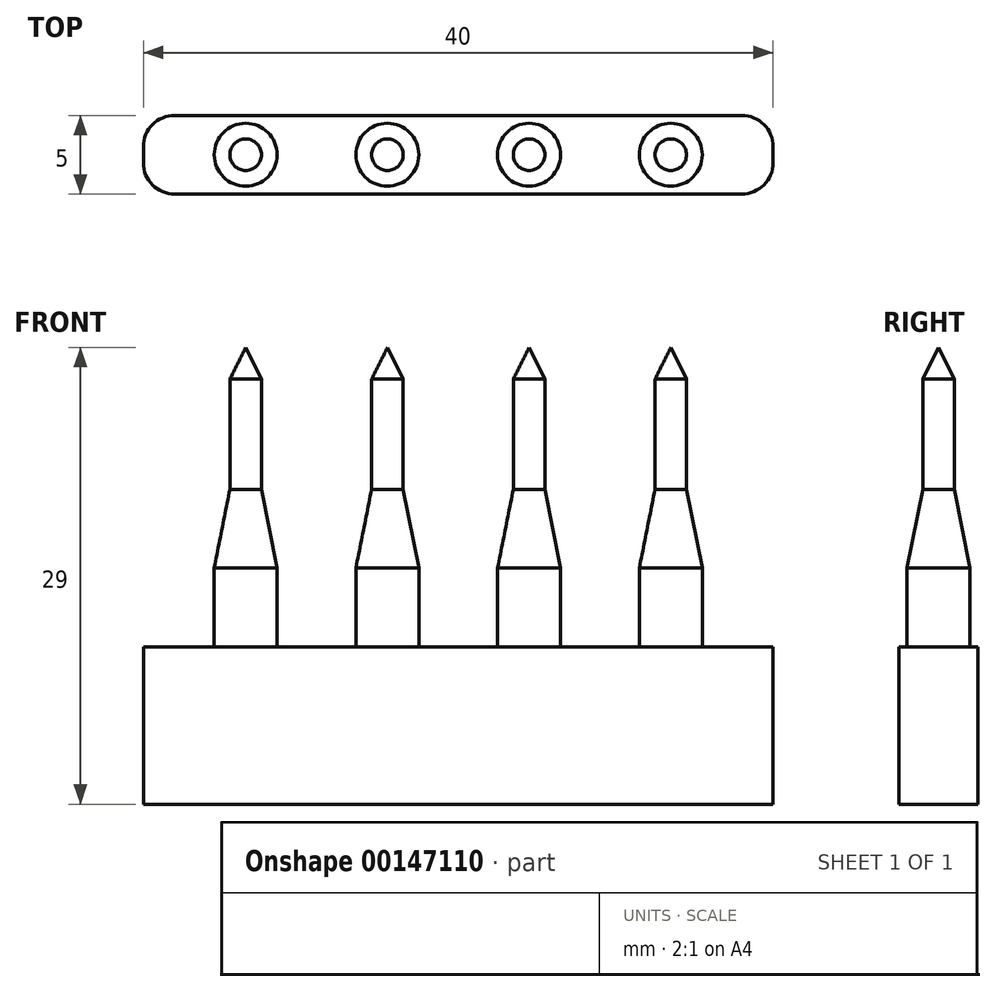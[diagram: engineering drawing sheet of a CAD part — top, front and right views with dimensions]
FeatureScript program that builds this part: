
annotation { "Feature Type Name" : "Feature", "Feature Type Description" : "" }
export const myFeature = defineFeature(function(context is Context, id is Id, definition is map)
    precondition{}
    {
        {
            var Q0;
            Q0=qCreatedBy(makeId("Top.planeOp"),FACE);
            var sketch = newSketch(context, id + "F0", { "sketchPlane" : qUnion([Q0])});
            skLineSegment(sketch, "E0", {"start": v(0, 0) * mm, "end": v(4.5, 0) * mm});
            skLineSegment(sketch, "E1", {"start": v(4.5, 0) * mm, "end": v(13.5, 0) * mm});
            skLineSegment(sketch, "E2", {"start": v(0, 0) * mm, "end": v(-4.5, 0) * mm});
            skLineSegment(sketch, "E3", {"start": v(-4.5, 0) * mm, "end": v(-13.5, 0) * mm});
            skCircle(sketch, "E4", {"center": v(-13.5, 0) * mm, "radius": 1 * mm});
            skCircle(sketch, "E5", {"center": v(-4.5, 0) * mm, "radius": 1 * mm});
            skCircle(sketch, "E6", {"center": v(4.5, 0) * mm, "radius": 1 * mm});
            skCircle(sketch, "E7", {"center": v(13.5, 0) * mm, "radius": 1 * mm});
            skLineSegment(sketch, "E8.bottom", {"start": v(20, 2.5) * mm, "end": v(-20, 2.5) * mm});
            skLineSegment(sketch, "E8.top", {"start": v(20, -2.5) * mm, "end": v(-20, -2.5) * mm});
            skLineSegment(sketch, "E8.left", {"start": v(20, 2.5) * mm, "end": v(20, -2.5) * mm});
            skLineSegment(sketch, "E8.right", {"start": v(-20, 2.5) * mm, "end": v(-20, -2.5) * mm});
            skPoint(sketch, "E8.middle", {"position": v(0, 0) * mm});
            skCircle(sketch, "E9", {"center": v(-13.5, 0) * mm, "radius": 2 * mm});
            skCircle(sketch, "E10", {"center": v(-4.5, 0) * mm, "radius": 2 * mm});
            skCircle(sketch, "E11", {"center": v(4.5, 0) * mm, "radius": 2 * mm});
            skCircle(sketch, "E12", {"center": v(13.5, 0) * mm, "radius": 2 * mm});
            skSolve(sketch);
        }
        {
            var Q0;
            {var subQ0=sQuery(id+"F0.wireOp",EDGE,"E8.left");Q0=makeQuery(id+"F0.imprint","IMPRINT",FACE,{"disambiguationData":[TD([[makeQuery(id+"F0.imprint","IMPRINT",EDGE,{"derivedFrom":subQ0}),-1.0]])]});}
            var Q1;
            {var subQ0=sQuery(id+"F0.wireOp",EDGE,"E8.right");Q1=makeQuery(id+"F0.imprint","IMPRINT",FACE,{"disambiguationData":[TD([[makeQuery(id+"F0.imprint","IMPRINT",EDGE,{"derivedFrom":subQ0}),1.0]])]});}
            var Q2;
            {var subQ3=sQuery(id+"F0.wireOp",EDGE,"E2");var subQ5=sQuery(id+"F0.wireOp",EDGE,"E0");var subQ6=makeQuery(id+"F0.imprint","INTERSECT",VERTEX,{"derivedFrom":[subQ5,subQ3]});Q2=makeQuery(id+"F0.imprint","IMPRINT",FACE,{"disambiguationData":[TD([[makeQuery(id+"F0.imprint","IMPRINT",EDGE,{"disambiguationData":[TD([[subQ6,-1.0]])],"derivedFrom":subQ5}),1.0]])]});}
            var Q3;
            {var subQ3=sQuery(id+"F0.wireOp",EDGE,"E2");var subQ7=sQuery(id+"F0.wireOp",EDGE,"E0");var subQ8=makeQuery(id+"F0.imprint","INTERSECT",VERTEX,{"derivedFrom":[subQ7,subQ3]});Q3=makeQuery(id+"F0.imprint","IMPRINT",FACE,{"disambiguationData":[TD([[makeQuery(id+"F0.imprint","IMPRINT",EDGE,{"disambiguationData":[TD([[subQ8,-1.0]])],"derivedFrom":subQ7}),-1.0]])]});}
            var Q4;
            {var subQ0=sQuery(id+"F0.wireOp",EDGE,"U3uNiEoL-ytFB-zz6d-zu6e-E4LWmO1OLc1b");var subQ1=sQuery(id+"F0.wireOp",EDGE,"E1");var subQ2=makeQuery(id+"F0.imprint","INTERSECT",VERTEX,{"derivedFrom":[subQ1,subQ0]});Q4=makeQuery(id+"F0.imprint","IMPRINT",FACE,{"disambiguationData":[TD([[makeQuery(id+"F0.imprint","IMPRINT",EDGE,{"disambiguationData":[TD([[subQ2,1.0]])],"derivedFrom":subQ1}),1.0]])]});}
            var Q5;
            {var subQ0=sQuery(id+"F0.wireOp",EDGE,"U3uNiEoL-ytFB-zz6d-zu6e-E4LWmO1OLc1b");var subQ1=sQuery(id+"F0.wireOp",EDGE,"E1");var subQ2=makeQuery(id+"F0.imprint","INTERSECT",VERTEX,{"derivedFrom":[subQ1,subQ0]});Q5=makeQuery(id+"F0.imprint","IMPRINT",FACE,{"disambiguationData":[TD([[makeQuery(id+"F0.imprint","IMPRINT",EDGE,{"disambiguationData":[TD([[subQ2,1.0]])],"derivedFrom":subQ1}),-1.0]])]});}
            var Q6;
            {var subQ0=sQuery(id+"F0.wireOp",EDGE,"ClDRhj1H-6xjR-YOIk-xAHQ-ztIX2t5JyYzg");var subQ1=sQuery(id+"F0.wireOp",EDGE,"E3");var subQ2=makeQuery(id+"F0.imprint","INTERSECT",VERTEX,{"derivedFrom":[subQ1,subQ0]});Q6=makeQuery(id+"F0.imprint","IMPRINT",FACE,{"disambiguationData":[TD([[makeQuery(id+"F0.imprint","IMPRINT",EDGE,{"disambiguationData":[TD([[subQ2,1.0]])],"derivedFrom":subQ1}),-1.0]])]});}
            var Q7;
            {var subQ0=sQuery(id+"F0.wireOp",EDGE,"ClDRhj1H-6xjR-YOIk-xAHQ-ztIX2t5JyYzg");var subQ1=sQuery(id+"F0.wireOp",EDGE,"E3");var subQ2=makeQuery(id+"F0.imprint","INTERSECT",VERTEX,{"derivedFrom":[subQ1,subQ0]});Q7=makeQuery(id+"F0.imprint","IMPRINT",FACE,{"disambiguationData":[TD([[makeQuery(id+"F0.imprint","IMPRINT",EDGE,{"disambiguationData":[TD([[subQ2,1.0]])],"derivedFrom":subQ1}),1.0]])]});}
            var Q8;
            Q8=makeQuery(id+"F0.imprint","IMPRINT",FACE,{"disambiguationData":[TD([[makeQuery(id+"F0.imprint","IMPRINT",EDGE,{"derivedFrom":sQuery(id+"F0.wireOp",EDGE,"E7")}),-1.0]])]});
            var Q9;
            {var subQ0=sQuery(id+"F0.wireOp",EDGE,"8HZm2u9n-6hcU-8h6m-0SvE-3ht0zT66AFrF");var subQ2=sQuery(id+"F0.wireOp",EDGE,"E0");var subQ3=makeQuery(id+"F0.imprint","INTERSECT",VERTEX,{"derivedFrom":[subQ2,subQ0]});Q9=makeQuery(id+"F0.imprint","IMPRINT",FACE,{"disambiguationData":[TD([[makeQuery(id+"F0.imprint","IMPRINT",EDGE,{"disambiguationData":[TD([[subQ3,-1.0]])],"derivedFrom":subQ2}),-1.0]])]});}
            var Q10;
            {var subQ1=sQuery(id+"F0.wireOp",EDGE,"E2");var subQ5=sQuery(id+"F0.wireOp",EDGE,"egIFAelI-ejJv-sLzS-e5zb-D6Cz2TTPKjOq");var subQ7=makeQuery(id+"F0.imprint","INTERSECT",VERTEX,{"derivedFrom":[subQ1,subQ5]});Q10=makeQuery(id+"F0.imprint","IMPRINT",FACE,{"disambiguationData":[TD([[makeQuery(id+"F0.imprint","IMPRINT",EDGE,{"disambiguationData":[TD([[subQ7,-1.0]])],"derivedFrom":subQ1}),1.0]])]});}
            var Q11;
            Q11=makeQuery(id+"F0.imprint","IMPRINT",FACE,{"disambiguationData":[TD([[makeQuery(id+"F0.imprint","IMPRINT",EDGE,{"derivedFrom":sQuery(id+"F0.wireOp",EDGE,"E4")}),-1.0]])]});
            var Q12;
            {var subQ0=sQuery(id+"F0.wireOp",EDGE,"egIFAelI-ejJv-sLzS-e5zb-D6Cz2TTPKjOq");var subQ2=sQuery(id+"F0.wireOp",EDGE,"E2");var subQ3=makeQuery(id+"F0.imprint","INTERSECT",VERTEX,{"derivedFrom":[subQ2,subQ0]});Q12=makeQuery(id+"F0.imprint","IMPRINT",FACE,{"disambiguationData":[TD([[makeQuery(id+"F0.imprint","IMPRINT",EDGE,{"disambiguationData":[TD([[subQ3,-1.0]])],"derivedFrom":subQ2}),-1.0]])]});}
            var Q13;
            {var subQ0=sQuery(id+"F0.wireOp",EDGE,"8HZm2u9n-6hcU-8h6m-0SvE-3ht0zT66AFrF");var subQ5=sQuery(id+"F0.wireOp",EDGE,"E0");var subQ8=makeQuery(id+"F0.imprint","INTERSECT",VERTEX,{"derivedFrom":[subQ5,subQ0]});Q13=makeQuery(id+"F0.imprint","IMPRINT",FACE,{"disambiguationData":[TD([[makeQuery(id+"F0.imprint","IMPRINT",EDGE,{"disambiguationData":[TD([[subQ8,-1.0]])],"derivedFrom":subQ5}),1.0]])]});}
            var Q14;
            Q14=makeQuery(id+"F0.imprint","IMPRINT",FACE,{"disambiguationData":[TD([[makeQuery(id+"F0.imprint","IMPRINT",EDGE,{"derivedFrom":sQuery(id+"F0.wireOp",EDGE,"E7")}),1.0]])]});
            var Q15;
            {var subQ0=sQuery(id+"F0.wireOp",EDGE,"E1");var subQ1=sQuery(id+"F0.wireOp",EDGE,"E0");var subQ2=makeQuery(id+"F0.imprint","INTERSECT",VERTEX,{"derivedFrom":[subQ1,subQ0]});Q15=makeQuery(id+"F0.imprint","IMPRINT",FACE,{"disambiguationData":[TD([[makeQuery(id+"F0.imprint","IMPRINT",EDGE,{"disambiguationData":[TD([[subQ2,1.0]])],"derivedFrom":subQ1}),-1.0]])]});}
            var Q16;
            {var subQ0=sQuery(id+"F0.wireOp",EDGE,"E3");var subQ1=sQuery(id+"F0.wireOp",EDGE,"E2");var subQ2=makeQuery(id+"F0.imprint","INTERSECT",VERTEX,{"derivedFrom":[subQ1,subQ0]});Q16=makeQuery(id+"F0.imprint","IMPRINT",FACE,{"disambiguationData":[TD([[makeQuery(id+"F0.imprint","IMPRINT",EDGE,{"disambiguationData":[TD([[subQ2,1.0]])],"derivedFrom":subQ1}),1.0]])]});}
            var Q17;
            Q17=makeQuery(id+"F0.imprint","IMPRINT",FACE,{"disambiguationData":[TD([[makeQuery(id+"F0.imprint","IMPRINT",EDGE,{"derivedFrom":sQuery(id+"F0.wireOp",EDGE,"E4")}),1.0]])]});
            var Q18;
            {var subQ0=sQuery(id+"F0.wireOp",EDGE,"E3");var subQ1=sQuery(id+"F0.wireOp",EDGE,"E2");var subQ2=makeQuery(id+"F0.imprint","INTERSECT",VERTEX,{"derivedFrom":[subQ1,subQ0]});Q18=makeQuery(id+"F0.imprint","IMPRINT",FACE,{"disambiguationData":[TD([[makeQuery(id+"F0.imprint","IMPRINT",EDGE,{"disambiguationData":[TD([[subQ2,1.0]])],"derivedFrom":subQ1}),-1.0]])]});}
            var Q19;
            {var subQ0=sQuery(id+"F0.wireOp",EDGE,"E1");var subQ1=sQuery(id+"F0.wireOp",EDGE,"E0");var subQ2=makeQuery(id+"F0.imprint","INTERSECT",VERTEX,{"derivedFrom":[subQ1,subQ0]});Q19=makeQuery(id+"F0.imprint","IMPRINT",FACE,{"disambiguationData":[TD([[makeQuery(id+"F0.imprint","IMPRINT",EDGE,{"disambiguationData":[TD([[subQ2,1.0]])],"derivedFrom":subQ1}),1.0]])]});}
            var Q20;
            {var subQ0=sQuery(id+"F0.wireOp",EDGE,"E10");var subQ1=sQuery(id+"F0.wireOp",EDGE,"E2");var subQ2=makeQuery(id+"F0.imprint","INTERSECT",VERTEX,{"derivedFrom":[subQ1,subQ0]});Q20=makeQuery(id+"F0.imprint","IMPRINT",FACE,{"disambiguationData":[TD([[makeQuery(id+"F0.imprint","IMPRINT",EDGE,{"disambiguationData":[TD([[subQ2,-1.0]])],"derivedFrom":subQ1}),1.0]])]});}
            var Q21;
            {var subQ0=sQuery(id+"F0.wireOp",EDGE,"E11");var subQ1=sQuery(id+"F0.wireOp",EDGE,"E0");var subQ2=makeQuery(id+"F0.imprint","INTERSECT",VERTEX,{"derivedFrom":[subQ1,subQ0]});Q21=makeQuery(id+"F0.imprint","IMPRINT",FACE,{"disambiguationData":[TD([[makeQuery(id+"F0.imprint","IMPRINT",EDGE,{"disambiguationData":[TD([[subQ2,-1.0]])],"derivedFrom":subQ1}),-1.0]])]});}
            var Q22;
            {var subQ0=sQuery(id+"F0.wireOp",EDGE,"E11");var subQ1=sQuery(id+"F0.wireOp",EDGE,"E0");var subQ2=makeQuery(id+"F0.imprint","INTERSECT",VERTEX,{"derivedFrom":[subQ1,subQ0]});Q22=makeQuery(id+"F0.imprint","IMPRINT",FACE,{"disambiguationData":[TD([[makeQuery(id+"F0.imprint","IMPRINT",EDGE,{"disambiguationData":[TD([[subQ2,-1.0]])],"derivedFrom":subQ1}),1.0]])]});}
            var Q23;
            {var subQ0=sQuery(id+"F0.wireOp",EDGE,"E10");var subQ1=sQuery(id+"F0.wireOp",EDGE,"E2");var subQ2=makeQuery(id+"F0.imprint","INTERSECT",VERTEX,{"derivedFrom":[subQ1,subQ0]});Q23=makeQuery(id+"F0.imprint","IMPRINT",FACE,{"disambiguationData":[TD([[makeQuery(id+"F0.imprint","IMPRINT",EDGE,{"disambiguationData":[TD([[subQ2,-1.0]])],"derivedFrom":subQ1}),-1.0]])]});}
            extrude(context, id + "F1", {"entities" : qUnion([Q0, Q1, Q2, Q3, Q4, Q5, Q6, Q7, Q8, Q9, Q10, Q11, Q12, Q13, Q14, Q15, Q16, Q17, Q18, Q19, Q20, Q21, Q22, Q23]), "oppositeDirection" : true, "depth" : 10 * mm, "offsetDistance" : 25 * mm});
        }
        {
            var Q0;
            Q0=qCreatedBy(makeId("Front.planeOp"),FACE);
            var sketch = newSketch(context, id + "F2", { "sketchPlane" : qUnion([Q0])});
            skLineSegment(sketch, "E13", {"start": v(0, 0) * mm, "end": v(4.5, 0) * mm});
            skLineSegment(sketch, "E14", {"start": v(4.5, 0) * mm, "end": v(13.5, 0) * mm});
            skLineSegment(sketch, "E15", {"start": v(0, 0) * mm, "end": v(-4.5, 0) * mm});
            skLineSegment(sketch, "E16", {"start": v(-4.5, 0) * mm, "end": v(-13.5, 0) * mm});
            skLineSegment(sketch, "E17", {"start": v(-13.5, 0) * mm, "end": v(-13.5, 5) * mm});
            skLineSegment(sketch, "E18", {"start": v(-13.5, 5) * mm, "end": v(-11.5, 5) * mm});
            skLineSegment(sketch, "E19", {"start": v(-13.5, 5) * mm, "end": v(-13.5, 10) * mm});
            skLineSegment(sketch, "E20", {"start": v(-13.5, 10) * mm, "end": v(-12.5, 10) * mm});
            skLineSegment(sketch, "E21", {"start": v(-12.5, 10) * mm, "end": v(-11.5, 5) * mm});
            skLineSegment(sketch, "E22", {"start": v(-4.5, 0) * mm, "end": v(-4.5, 10) * mm});
            skLineSegment(sketch, "E23", {"start": v(-4.5, 10) * mm, "end": v(-3.5, 10) * mm});
            skLineSegment(sketch, "E24", {"start": v(-4.5, 0) * mm, "end": v(-4.5, 5) * mm});
            skLineSegment(sketch, "E25", {"start": v(-4.5, 5) * mm, "end": v(-2.5, 5) * mm});
            skLineSegment(sketch, "E26", {"start": v(-2.5, 5) * mm, "end": v(-3.5, 10) * mm});
            skLineSegment(sketch, "E27.MirrorCS", {"start": v(4.5, 5) * mm, "end": v(2.5, 5) * mm});
            skLineSegment(sketch, "E28.MirrorCS", {"start": v(2.5, 5) * mm, "end": v(3.5, 10) * mm});
            skLineSegment(sketch, "E29.MirrorCS", {"start": v(4.5, 10) * mm, "end": v(3.5, 10) * mm});
            skLineSegment(sketch, "E30", {"start": v(-12.5, 10) * mm, "end": v(-12.5, 17) * mm});
            skLineSegment(sketch, "E31", {"start": v(-13.5, 10) * mm, "end": v(-13.5, 19) * mm});
            skLineSegment(sketch, "E32", {"start": v(-13.5, 19) * mm, "end": v(-12.5, 17) * mm});
            skLineSegment(sketch, "E33", {"start": v(-4.5, 10) * mm, "end": v(-4.5, 19) * mm});
            skLineSegment(sketch, "E34", {"start": v(-3.5, 10) * mm, "end": v(-3.5, 17) * mm});
            skLineSegment(sketch, "E35", {"start": v(-3.5, 17) * mm, "end": v(-4.5, 19) * mm});
            skLineSegment(sketch, "E36.MirrorCS", {"start": v(3.5, 10) * mm, "end": v(3.5, 17) * mm});
            skLineSegment(sketch, "E37.MirrorCS", {"start": v(4.5, 10) * mm, "end": v(4.5, 19) * mm});
            skLineSegment(sketch, "E38.MirrorCS", {"start": v(3.5, 17) * mm, "end": v(4.5, 19) * mm});
            skLineSegment(sketch, "E39.MirrorCS", {"start": v(4.5, 0) * mm, "end": v(4.5, 10) * mm});
            skLineSegment(sketch, "E40.MirrorCS", {"start": v(13.5, 10) * mm, "end": v(13.5, 19) * mm});
            skLineSegment(sketch, "E41.MirrorCS", {"start": v(13.5, 19) * mm, "end": v(12.5, 17) * mm});
            skLineSegment(sketch, "E42.MirrorCS", {"start": v(12.5, 10) * mm, "end": v(12.5, 17) * mm});
            skLineSegment(sketch, "E43.MirrorCS", {"start": v(12.5, 10) * mm, "end": v(11.5, 5) * mm});
            skLineSegment(sketch, "E44.MirrorCS", {"start": v(13.5, 5) * mm, "end": v(13.5, 10) * mm});
            skLineSegment(sketch, "E45.MirrorCS", {"start": v(13.5, 5) * mm, "end": v(11.5, 5) * mm});
            skSolve(sketch);
        }
        {
            var Q0;
            Q0=makeQuery(id+"F0.imprint","IMPRINT",FACE,{"disambiguationData":[TD([[makeQuery(id+"F0.imprint","IMPRINT",EDGE,{"derivedFrom":sQuery(id+"F0.wireOp",EDGE,"E4")}),-1.0]])]});
            var Q1;
            {var subQ1=sQuery(id+"F0.wireOp",EDGE,"E2");var subQ5=sQuery(id+"F0.wireOp",EDGE,"egIFAelI-ejJv-sLzS-e5zb-D6Cz2TTPKjOq");var subQ7=makeQuery(id+"F0.imprint","INTERSECT",VERTEX,{"derivedFrom":[subQ1,subQ5]});Q1=makeQuery(id+"F0.imprint","IMPRINT",FACE,{"disambiguationData":[TD([[makeQuery(id+"F0.imprint","IMPRINT",EDGE,{"disambiguationData":[TD([[subQ7,-1.0]])],"derivedFrom":subQ1}),1.0]])]});}
            var Q2;
            {var subQ0=sQuery(id+"F0.wireOp",EDGE,"egIFAelI-ejJv-sLzS-e5zb-D6Cz2TTPKjOq");var subQ2=sQuery(id+"F0.wireOp",EDGE,"E2");var subQ3=makeQuery(id+"F0.imprint","INTERSECT",VERTEX,{"derivedFrom":[subQ2,subQ0]});Q2=makeQuery(id+"F0.imprint","IMPRINT",FACE,{"disambiguationData":[TD([[makeQuery(id+"F0.imprint","IMPRINT",EDGE,{"disambiguationData":[TD([[subQ3,-1.0]])],"derivedFrom":subQ2}),-1.0]])]});}
            var Q3;
            {var subQ0=sQuery(id+"F0.wireOp",EDGE,"8HZm2u9n-6hcU-8h6m-0SvE-3ht0zT66AFrF");var subQ2=sQuery(id+"F0.wireOp",EDGE,"E0");var subQ3=makeQuery(id+"F0.imprint","INTERSECT",VERTEX,{"derivedFrom":[subQ2,subQ0]});Q3=makeQuery(id+"F0.imprint","IMPRINT",FACE,{"disambiguationData":[TD([[makeQuery(id+"F0.imprint","IMPRINT",EDGE,{"disambiguationData":[TD([[subQ3,-1.0]])],"derivedFrom":subQ2}),-1.0]])]});}
            var Q4;
            {var subQ0=sQuery(id+"F0.wireOp",EDGE,"8HZm2u9n-6hcU-8h6m-0SvE-3ht0zT66AFrF");var subQ5=sQuery(id+"F0.wireOp",EDGE,"E0");var subQ8=makeQuery(id+"F0.imprint","INTERSECT",VERTEX,{"derivedFrom":[subQ5,subQ0]});Q4=makeQuery(id+"F0.imprint","IMPRINT",FACE,{"disambiguationData":[TD([[makeQuery(id+"F0.imprint","IMPRINT",EDGE,{"disambiguationData":[TD([[subQ8,-1.0]])],"derivedFrom":subQ5}),1.0]])]});}
            var Q5;
            Q5=makeQuery(id+"F0.imprint","IMPRINT",FACE,{"disambiguationData":[TD([[makeQuery(id+"F0.imprint","IMPRINT",EDGE,{"derivedFrom":sQuery(id+"F0.wireOp",EDGE,"E7")}),-1.0]])]});
            var Q6;
            {var subQ0=sQuery(id+"F0.wireOp",EDGE,"E1");var subQ1=sQuery(id+"F0.wireOp",EDGE,"E0");var subQ2=makeQuery(id+"F0.imprint","INTERSECT",VERTEX,{"derivedFrom":[subQ1,subQ0]});Q6=makeQuery(id+"F0.imprint","IMPRINT",FACE,{"disambiguationData":[TD([[makeQuery(id+"F0.imprint","IMPRINT",EDGE,{"disambiguationData":[TD([[subQ2,1.0]])],"derivedFrom":subQ1}),-1.0]])]});}
            var Q7;
            Q7=makeQuery(id+"F0.imprint","IMPRINT",FACE,{"disambiguationData":[TD([[makeQuery(id+"F0.imprint","IMPRINT",EDGE,{"derivedFrom":sQuery(id+"F0.wireOp",EDGE,"E7")}),1.0]])]});
            var Q8;
            {var subQ0=sQuery(id+"F0.wireOp",EDGE,"E1");var subQ1=sQuery(id+"F0.wireOp",EDGE,"E0");var subQ2=makeQuery(id+"F0.imprint","INTERSECT",VERTEX,{"derivedFrom":[subQ1,subQ0]});Q8=makeQuery(id+"F0.imprint","IMPRINT",FACE,{"disambiguationData":[TD([[makeQuery(id+"F0.imprint","IMPRINT",EDGE,{"disambiguationData":[TD([[subQ2,1.0]])],"derivedFrom":subQ1}),1.0]])]});}
            var Q9;
            {var subQ0=sQuery(id+"F0.wireOp",EDGE,"E3");var subQ1=sQuery(id+"F0.wireOp",EDGE,"E2");var subQ2=makeQuery(id+"F0.imprint","INTERSECT",VERTEX,{"derivedFrom":[subQ1,subQ0]});Q9=makeQuery(id+"F0.imprint","IMPRINT",FACE,{"disambiguationData":[TD([[makeQuery(id+"F0.imprint","IMPRINT",EDGE,{"disambiguationData":[TD([[subQ2,1.0]])],"derivedFrom":subQ1}),1.0]])]});}
            var Q10;
            {var subQ0=sQuery(id+"F0.wireOp",EDGE,"E3");var subQ1=sQuery(id+"F0.wireOp",EDGE,"E2");var subQ2=makeQuery(id+"F0.imprint","INTERSECT",VERTEX,{"derivedFrom":[subQ1,subQ0]});Q10=makeQuery(id+"F0.imprint","IMPRINT",FACE,{"disambiguationData":[TD([[makeQuery(id+"F0.imprint","IMPRINT",EDGE,{"disambiguationData":[TD([[subQ2,1.0]])],"derivedFrom":subQ1}),-1.0]])]});}
            var Q11;
            Q11=makeQuery(id+"F0.imprint","IMPRINT",FACE,{"disambiguationData":[TD([[makeQuery(id+"F0.imprint","IMPRINT",EDGE,{"derivedFrom":sQuery(id+"F0.wireOp",EDGE,"E4")}),1.0]])]});
            var Q12;
            {var subQ0=sQuery(id+"F0.wireOp",EDGE,"E10");var subQ1=sQuery(id+"F0.wireOp",EDGE,"E2");var subQ2=makeQuery(id+"F0.imprint","INTERSECT",VERTEX,{"derivedFrom":[subQ1,subQ0]});Q12=makeQuery(id+"F0.imprint","IMPRINT",FACE,{"disambiguationData":[TD([[makeQuery(id+"F0.imprint","IMPRINT",EDGE,{"disambiguationData":[TD([[subQ2,-1.0]])],"derivedFrom":subQ1}),1.0]])]});}
            var Q13;
            {var subQ0=sQuery(id+"F0.wireOp",EDGE,"E10");var subQ1=sQuery(id+"F0.wireOp",EDGE,"E2");var subQ2=makeQuery(id+"F0.imprint","INTERSECT",VERTEX,{"derivedFrom":[subQ1,subQ0]});Q13=makeQuery(id+"F0.imprint","IMPRINT",FACE,{"disambiguationData":[TD([[makeQuery(id+"F0.imprint","IMPRINT",EDGE,{"disambiguationData":[TD([[subQ2,-1.0]])],"derivedFrom":subQ1}),-1.0]])]});}
            var Q14;
            {var subQ0=sQuery(id+"F0.wireOp",EDGE,"E11");var subQ1=sQuery(id+"F0.wireOp",EDGE,"E0");var subQ2=makeQuery(id+"F0.imprint","INTERSECT",VERTEX,{"derivedFrom":[subQ1,subQ0]});Q14=makeQuery(id+"F0.imprint","IMPRINT",FACE,{"disambiguationData":[TD([[makeQuery(id+"F0.imprint","IMPRINT",EDGE,{"disambiguationData":[TD([[subQ2,-1.0]])],"derivedFrom":subQ1}),1.0]])]});}
            var Q15;
            {var subQ0=sQuery(id+"F0.wireOp",EDGE,"E11");var subQ1=sQuery(id+"F0.wireOp",EDGE,"E0");var subQ2=makeQuery(id+"F0.imprint","INTERSECT",VERTEX,{"derivedFrom":[subQ1,subQ0]});Q15=makeQuery(id+"F0.imprint","IMPRINT",FACE,{"disambiguationData":[TD([[makeQuery(id+"F0.imprint","IMPRINT",EDGE,{"disambiguationData":[TD([[subQ2,-1.0]])],"derivedFrom":subQ1}),-1.0]])]});}
            extrude(context, id + "F3", {"entities" : qUnion([Q0, Q1, Q2, Q3, Q4, Q5, Q6, Q7, Q8, Q9, Q10, Q11, Q12, Q13, Q14, Q15]), "operationType" : NewBodyOperationType.ADD, "depth" : 5 * mm, "offsetDistance" : 25 * mm});
        }
        {
            var Q0;
            Q0=makeQuery(id+"F2.imprint","IMPRINT",FACE,{"disambiguationData":[TD([[makeQuery(id+"F2.imprint","IMPRINT",EDGE,{"derivedFrom":sQuery(id+"F2.wireOp",EDGE,"E20")}),1.0]])]});
            var Q1;
            Q1=makeQuery(id+"F2.imprint","IMPRINT",FACE,{"disambiguationData":[TD([[makeQuery(id+"F2.imprint","IMPRINT",EDGE,{"derivedFrom":sQuery(id+"F2.wireOp",EDGE,"E18")}),1.0]])]});
            var Q2;
            Q2=sQuery(id+"F2.wireOp",EDGE,"E31");
            var Q3;
            Q3=sQuery(id+"F2.wireOp",EDGE,"E19");
            var Q4;
            Q4=sQuery(id+"F2.wireOp",EDGE,"E31");
            revolve(context, id + "F4", {"operationType" : NewBodyOperationType.ADD, "surfaceOperationType" : NewSurfaceOperationType.NEW, "entities" : qUnion([Q0, Q1]), "surfaceEntities" : qUnion([Q2, Q3]), "axis" : qUnion([Q4]), "revolveType" : RevolveType.FULL});
        }
        {
            var Q0;
            Q0=makeQuery(id+"F2.imprint","IMPRINT",FACE,{"disambiguationData":[TD([[makeQuery(id+"F2.imprint","IMPRINT",EDGE,{"derivedFrom":sQuery(id+"F2.wireOp",EDGE,"E23")}),1.0]])]});
            var Q1;
            Q1=makeQuery(id+"F2.imprint","IMPRINT",FACE,{"disambiguationData":[TD([[makeQuery(id+"F2.imprint","IMPRINT",EDGE,{"derivedFrom":sQuery(id+"F2.wireOp",EDGE,"E22")}),-1.0]])]});
            var Q2;
            Q2=sQuery(id+"F2.wireOp",EDGE,"E33");
            revolve(context, id + "F5", {"operationType" : NewBodyOperationType.ADD, "surfaceOperationType" : NewSurfaceOperationType.NEW, "entities" : qUnion([Q0, Q1]), "axis" : qUnion([Q2]), "revolveType" : RevolveType.FULL});
        }
        {
            var Q0;
            {var subQ0=sQuery(id+"F2.wireOp",EDGE,"E27.MirrorCS");Q0=makeQuery(id+"F2.imprint","IMPRINT",FACE,{"disambiguationData":[TD([[makeQuery(id+"F2.imprint","IMPRINT",EDGE,{"derivedFrom":subQ0}),-1.0]])]});}
            var Q1;
            Q1=makeQuery(id+"F2.imprint","IMPRINT",FACE,{"disambiguationData":[TD([[makeQuery(id+"F2.imprint","IMPRINT",EDGE,{"derivedFrom":sQuery(id+"F2.wireOp",EDGE,"E29.MirrorCS")}),-1.0]])]});
            var Q2;
            Q2=sQuery(id+"F2.wireOp",EDGE,"E37.MirrorCS");
            revolve(context, id + "F6", {"operationType" : NewBodyOperationType.ADD, "surfaceOperationType" : NewSurfaceOperationType.NEW, "entities" : qUnion([Q0, Q1]), "axis" : qUnion([Q2]), "revolveType" : RevolveType.FULL});
        }
        {
            var Q0;
            Q0=makeQuery(id+"F2.imprint","IMPRINT",FACE,{"disambiguationData":[TD([[makeQuery(id+"F2.imprint","IMPRINT",EDGE,{"derivedFrom":sQuery(id+"F2.wireOp",EDGE,"E40.MirrorCS")}),1.0]])]});
            var Q1;
            Q1=sQuery(id+"F2.wireOp",EDGE,"E40.MirrorCS");
            revolve(context, id + "F7", {"operationType" : NewBodyOperationType.ADD, "surfaceOperationType" : NewSurfaceOperationType.NEW, "entities" : qUnion([Q0]), "axis" : qUnion([Q1]), "revolveType" : RevolveType.FULL});
        }
        {
            var Q0;
            Q0=makeQuery(id+"F1.opExtrude","SWEPT_EDGE",EDGE,{"disambiguationData":[OSD([sQuery(id+"F0.wireOp",EDGE,"E8.top"),sQuery(id+"F0.wireOp",EDGE,"E8.right")])]});
            var Q1;
            Q1=makeQuery(id+"F1.opExtrude","SWEPT_EDGE",EDGE,{"disambiguationData":[OSD([sQuery(id+"F0.wireOp",EDGE,"E8.bottom"),sQuery(id+"F0.wireOp",EDGE,"E8.right")])]});
            var Q2;
            Q2=makeQuery(id+"F1.opExtrude","SWEPT_EDGE",EDGE,{"disambiguationData":[OSD([sQuery(id+"F0.wireOp",EDGE,"E8.top"),sQuery(id+"F0.wireOp",EDGE,"E8.left")])]});
            var Q3;
            Q3=makeQuery(id+"F1.opExtrude","SWEPT_EDGE",EDGE,{"disambiguationData":[OSD([sQuery(id+"F0.wireOp",EDGE,"E8.bottom"),sQuery(id+"F0.wireOp",EDGE,"E8.left")])]});
            fillet(context, id + "F8", {"entities" : qUnion([Q0, Q1, Q2, Q3]), "radius" : 2 * mm, "tangentPropagation" : true, "allowEdgeOverflow" : false});
        }
    });
